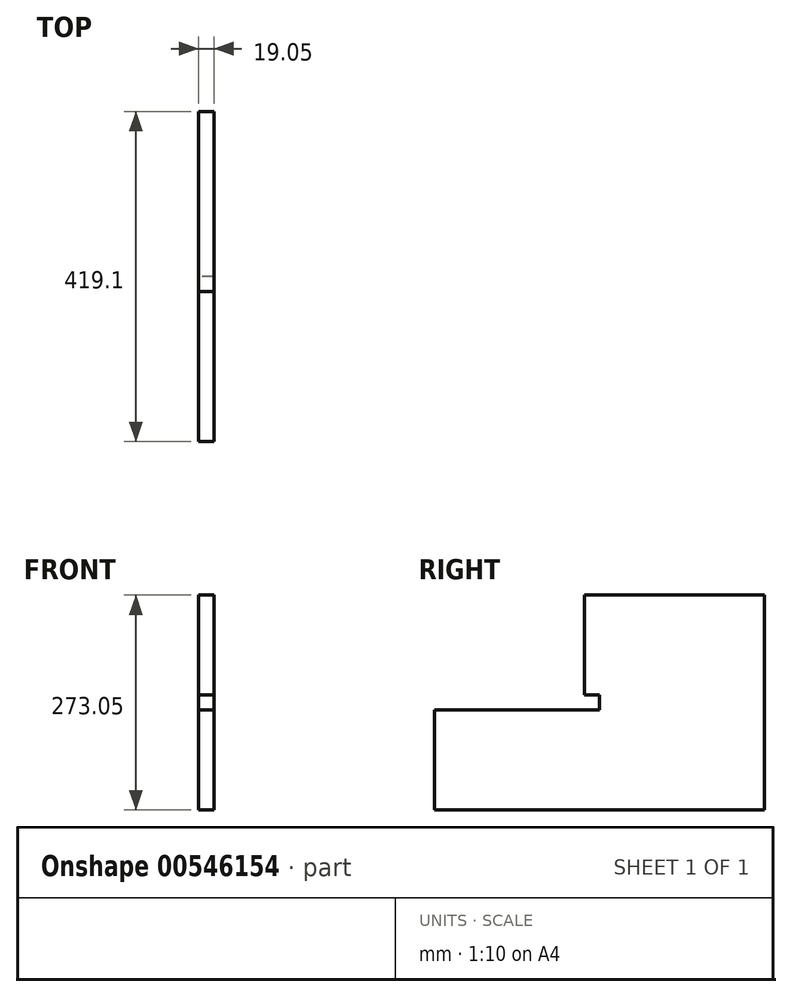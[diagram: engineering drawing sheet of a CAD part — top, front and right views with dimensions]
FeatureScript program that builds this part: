
annotation { "Feature Type Name" : "Feature", "Feature Type Description" : "" }
export const myFeature = defineFeature(function(context is Context, id is Id, definition is map)
    precondition{}
    {
        {
            var Q0;
            Q0=qCreatedBy(makeId("Right.planeOp"),FACE);
            var sketch = newSketch(context, id + "F0", { "sketchPlane" : qUnion([Q0])});
            skLineSegment(sketch, "E0.bottom", {"start": v(0, 0) * mm, "end": v(228.6, 0) * mm});
            skLineSegment(sketch, "E0.top", {"start": v(0, 146.05) * mm, "end": v(228.6, 146.05) * mm});
            skLineSegment(sketch, "E0.left", {"start": v(0, 0) * mm, "end": v(0, 146.05) * mm});
            skLineSegment(sketch, "E0.right", {"start": v(228.6, 0) * mm, "end": v(228.6, 146.05) * mm});
            skLineSegment(sketch, "E1.bottom", {"start": v(-190.5, 0) * mm, "end": v(228.6, 0) * mm});
            skLineSegment(sketch, "E1.top", {"start": v(-190.5, -127) * mm, "end": v(228.6, -127) * mm});
            skLineSegment(sketch, "E1.left", {"start": v(-190.5, 0) * mm, "end": v(-190.5, -127) * mm});
            skLineSegment(sketch, "E1.right", {"start": v(228.6, 0) * mm, "end": v(228.6, -127) * mm});
            skLineSegment(sketch, "E2", {"start": v(0, 0) * mm, "end": v(0, 19.05) * mm});
            skLineSegment(sketch, "E3", {"start": v(0, 19.05) * mm, "end": v(19.05, 19.05) * mm});
            skLineSegment(sketch, "E4", {"start": v(19.05, 19.05) * mm, "end": v(19.05, 0) * mm});
            skSolve(sketch);
        }
        {
            var Q0;
            Q0=makeQuery(id+"F0.imprint","IMPRINT",FACE,{"disambiguationData":[TD([[makeQuery(id+"F0.imprint","IMPRINT",EDGE,{"derivedFrom":sQuery(id+"F0.wireOp",EDGE,"E0.top")}),-1.0]])]});
            var Q1;
            Q1=makeQuery(id+"F0.imprint","IMPRINT",FACE,{"disambiguationData":[TD([[makeQuery(id+"F0.imprint","IMPRINT",EDGE,{"derivedFrom":sQuery(id+"F0.wireOp",EDGE,"E1.top")}),1.0]])]});
            extrude(context, id + "F1", {"entities" : qUnion([Q0, Q1]), "depth" : 19.05 * mm, "offsetDistance" : 25.4 * mm});
        }
    });
